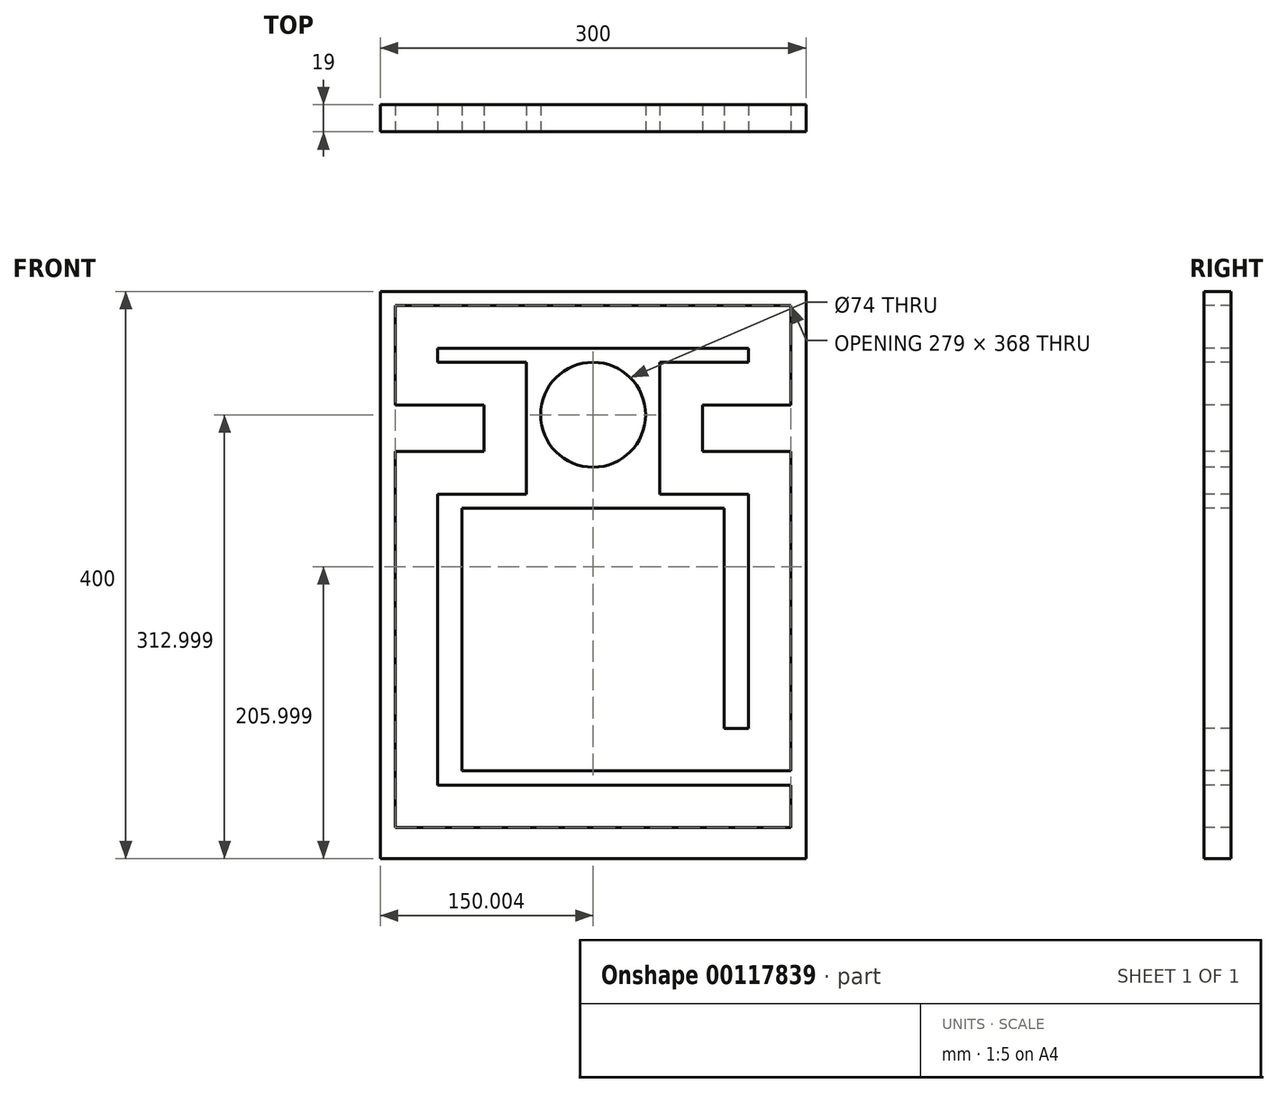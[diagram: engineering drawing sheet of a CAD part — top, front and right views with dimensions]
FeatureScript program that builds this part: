
annotation { "Feature Type Name" : "Feature", "Feature Type Description" : "" }
export const myFeature = defineFeature(function(context is Context, id is Id, definition is map)
    precondition{}
    {
        {
            var Q0;
            Q0=qCreatedBy(makeId("Front.planeOp"),FACE);
            var sketch = newSketch(context, id + "F0", { "sketchPlane" : qUnion([Q0])});
            skLineSegment(sketch, "E0.bottom", {"start": v(-161.3, 309.05) * mm, "end": v(138.7, 309.05) * mm});
            skLineSegment(sketch, "E0.top", {"start": v(-161.3, -90.95) * mm, "end": v(138.7, -90.95) * mm});
            skLineSegment(sketch, "E0.left", {"start": v(-161.3, 309.05) * mm, "end": v(-161.3, -90.95) * mm});
            skLineSegment(sketch, "E0.right", {"start": v(138.7, 309.05) * mm, "end": v(138.7, -90.95) * mm});
            skLineSegment(sketch, "E1.left", {"start": v(-161.3, 309.05) * mm, "end": v(-161.3, 309.05) * mm});
            skLineSegment(sketch, "E1.right", {"start": v(138.7, 309.05) * mm, "end": v(138.7, 309.05) * mm});
            skSolve(sketch);
        }
        {
            var Q0;
            Q0 = qSketchRegion(id + "F0", true);
            extrude(context, id + "F1", {"entities" : qUnion([Q0]), "depth" : 19 * mm});
        }
        {
            var Q0;
            Q0=makeQuery(id+"F1.opExtrude","CAP_FACE",FACE,{"disambiguationData":[OSD([sQuery(id+"F0.wireOp",EDGE,"E0.top"),sQuery(id+"F0.wireOp",EDGE,"E0.left"),sQuery(id+"F0.wireOp",EDGE,"E0.right"),sQuery(id+"F0.wireOp",EDGE,"E0.bottom")])],"isStart":false});
            var sketch = newSketch(context, id + "F2", { "sketchPlane" : qUnion([Q0])});
            skCircle(sketch, "E2", {"center": v(-11.3, 222.05) * mm, "radius": 37 * mm});
            skPoint(sketch, "E2.centerSnap0", {"position": v(-11.3, 309.05) * mm});
            skLineSegment(sketch, "E3", {"start": v(128.2, -38.95) * mm, "end": v(128.2, -68.95) * mm});
            skLineSegment(sketch, "E4", {"start": v(128.2, -68.95) * mm, "end": v(-150.8, -68.95) * mm});
            skLineSegment(sketch, "E5", {"start": v(-150.8, -68.95) * mm, "end": v(-150.8, 196.05) * mm});
            skLineSegment(sketch, "E6", {"start": v(-150.8, 196.05) * mm, "end": v(-88.3, 196.05) * mm});
            skLineSegment(sketch, "E7", {"start": v(-88.3, 196.05) * mm, "end": v(-88.3, 229.05) * mm});
            skLineSegment(sketch, "E8", {"start": v(-88.3, 229.05) * mm, "end": v(-150.8, 229.05) * mm});
            skLineSegment(sketch, "E9", {"start": v(-150.8, 229.05) * mm, "end": v(-150.8, 299.05) * mm});
            skLineSegment(sketch, "E10", {"start": v(-150.8, 299.05) * mm, "end": v(128.2, 299.05) * mm});
            skLineSegment(sketch, "E11", {"start": v(128.2, 299.05) * mm, "end": v(128.2, 229.05) * mm});
            skLineSegment(sketch, "E12", {"start": v(128.2, 229.05) * mm, "end": v(65.7, 229.05) * mm});
            skLineSegment(sketch, "E13", {"start": v(65.7, 229.05) * mm, "end": v(65.7, 196.05) * mm});
            skLineSegment(sketch, "E14", {"start": v(65.7, 196.05) * mm, "end": v(128.2, 196.05) * mm});
            skLineSegment(sketch, "E15", {"start": v(128.2, 196.05) * mm, "end": v(128.2, -28.95) * mm});
            skLineSegment(sketch, "E16", {"start": v(128.2, -28.95) * mm, "end": v(-103.8, -28.95) * mm});
            skLineSegment(sketch, "E17", {"start": v(-103.8, -28.95) * mm, "end": v(-103.8, 156.05) * mm});
            skLineSegment(sketch, "E18", {"start": v(-103.8, 156.05) * mm, "end": v(81.2, 156.05) * mm});
            skLineSegment(sketch, "E19", {"start": v(81.2, 156.05) * mm, "end": v(81.2, 1.05) * mm});
            skLineSegment(sketch, "E20", {"start": v(81.2, 1.05) * mm, "end": v(98.2, 1.05) * mm});
            skLineSegment(sketch, "E21", {"start": v(98.2, 1.05) * mm, "end": v(98.2, 166.05) * mm});
            skLineSegment(sketch, "E22", {"start": v(98.2, 166.05) * mm, "end": v(35.7, 166.05) * mm});
            skLineSegment(sketch, "E23", {"start": v(35.7, 166.05) * mm, "end": v(35.7, 259.05) * mm});
            skLineSegment(sketch, "E24", {"start": v(35.7, 259.05) * mm, "end": v(98.2, 259.05) * mm});
            skLineSegment(sketch, "E25", {"start": v(98.2, 259.05) * mm, "end": v(98.2, 269.05) * mm});
            skLineSegment(sketch, "E26", {"start": v(98.2, 269.05) * mm, "end": v(-120.8, 269.05) * mm});
            skLineSegment(sketch, "E27", {"start": v(-120.8, 269.05) * mm, "end": v(-120.8, 259.05) * mm});
            skLineSegment(sketch, "E28", {"start": v(-120.8, 259.05) * mm, "end": v(-58.3, 259.05) * mm});
            skLineSegment(sketch, "E29", {"start": v(-58.3, 259.05) * mm, "end": v(-58.3, 166.05) * mm});
            skLineSegment(sketch, "E30", {"start": v(-58.3, 166.05) * mm, "end": v(-120.8, 166.05) * mm});
            skLineSegment(sketch, "E31", {"start": v(-120.8, 166.05) * mm, "end": v(-120.8, -38.95) * mm});
            skLineSegment(sketch, "E32", {"start": v(-120.8, -38.95) * mm, "end": v(128.2, -38.95) * mm});
            skSolve(sketch);
        }
        {
            var Q0;
            Q0 = qSketchRegion(id + "F2", true);
            var Q1;
            Q1=makeQuery(id+"F2.imprint","IMPRINT",FACE,{"disambiguationData":[TD([[makeQuery(id+"F2.imprint","IMPRINT",EDGE,{"derivedFrom":sQuery(id+"F2.wireOp",EDGE,"E3")}),-1.0]])]});
            extrude(context, id + "F3", {"entities" : qUnion([Q0, Q1]), "operationType" : NewBodyOperationType.REMOVE, "oppositeDirection" : true, "depth" : 19 * mm});
        }
    });
